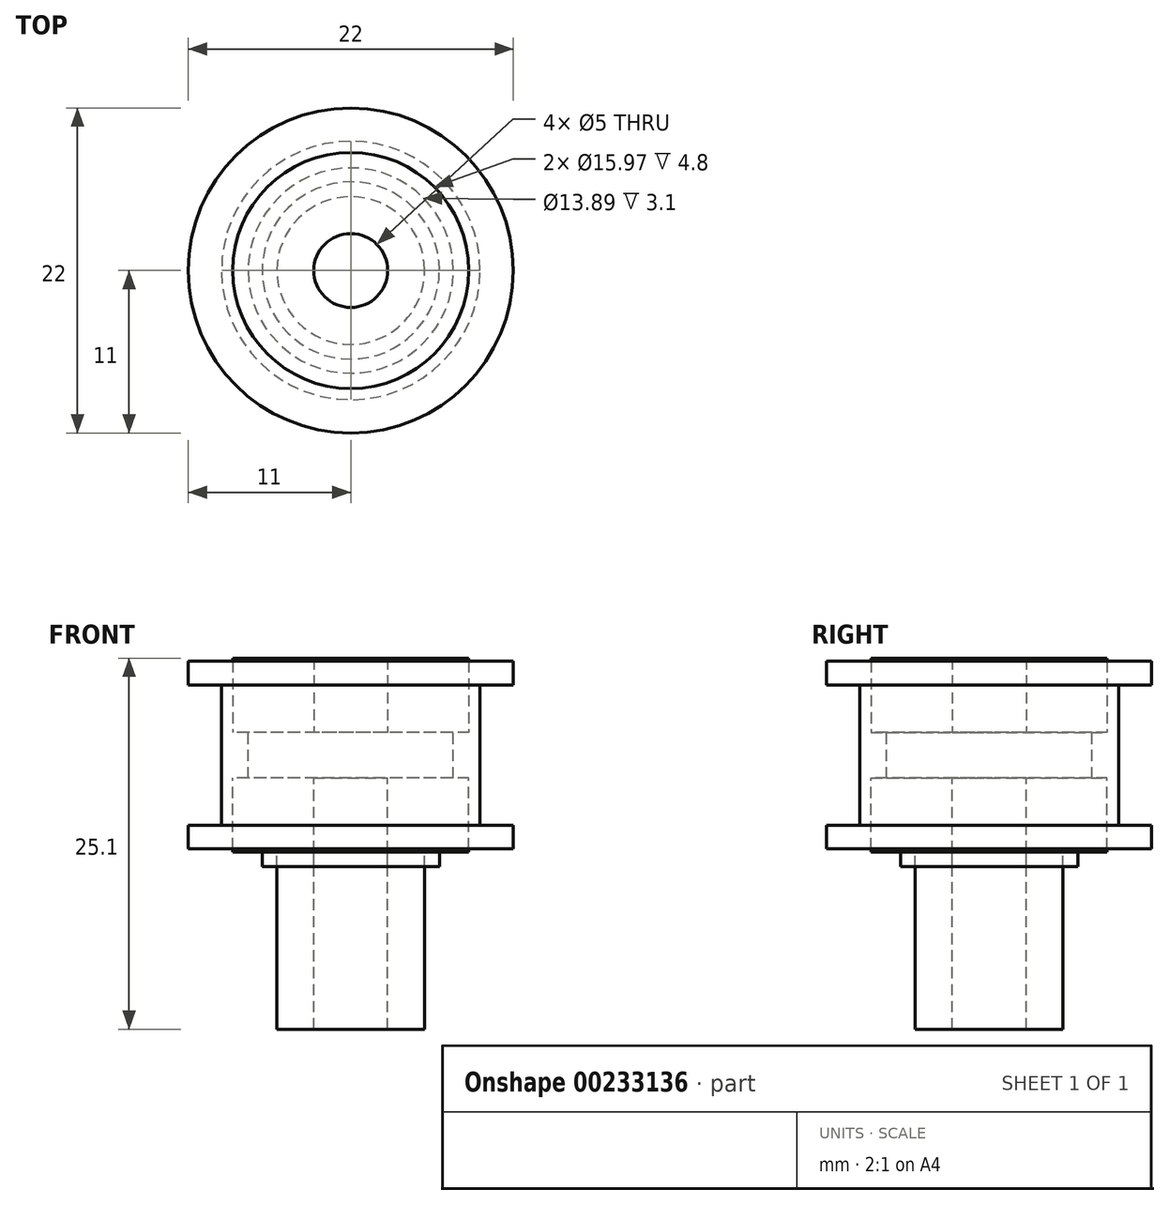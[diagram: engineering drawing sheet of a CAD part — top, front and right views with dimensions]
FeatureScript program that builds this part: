
annotation { "Feature Type Name" : "Feature", "Feature Type Description" : "" }
export const myFeature = defineFeature(function(context is Context, id is Id, definition is map)
    precondition{}
    {
        {
            var Q0;
            Q0=qCreatedBy(makeId("Right.planeOp"),FACE);
            var sketch = newSketch(context, id + "F0", { "sketchPlane" : qUnion([Q0])});
            skLineSegment(sketch, "E0", {"start": v(11, 6.35) * mm, "end": v(7.99, 6.35) * mm});
            skLineSegment(sketch, "E1", {"start": v(7.99, 6.35) * mm, "end": v(7.99, 1.55) * mm});
            skLineSegment(sketch, "E2", {"start": v(7.99, 1.55) * mm, "end": v(6.95, 1.55) * mm});
            skLineSegment(sketch, "E3", {"start": v(6.95, 1.55) * mm, "end": v(6.95, 0) * mm});
            skLineSegment(sketch, "E4", {"start": v(8.75, 0) * mm, "end": v(8.75, 4.75) * mm});
            skLineSegment(sketch, "E5", {"start": v(8.75, 4.75) * mm, "end": v(11, 4.75) * mm});
            skLineSegment(sketch, "E6", {"start": v(11, 4.75) * mm, "end": v(11, 6.35) * mm});
            skLineSegment(sketch, "E7", {"start": v(0, 6.35) * mm, "end": v(0, -6.95) * mm, "construction": true});
            skLineSegment(sketch, "E8", {"start": v(0, 0) * mm, "end": v(8.75, 0) * mm, "construction": true});
            skPoint(sketch, "E8.endSnap0", {"position": v(8.75, 0) * mm});
            skPoint(sketch, "E8.endSnap1", {"position": v(6.95, 0) * mm});
            skLineSegment(sketch, "E9.MirrorCS", {"start": v(7.99, -1.55) * mm, "end": v(6.95, -1.55) * mm});
            skLineSegment(sketch, "E10.MirrorCS", {"start": v(8.75, -4.75) * mm, "end": v(11, -4.75) * mm});
            skLineSegment(sketch, "E11.MirrorCS", {"start": v(8.75, 0) * mm, "end": v(8.75, -4.75) * mm});
            skLineSegment(sketch, "E12.MirrorCS", {"start": v(7.99, -6.35) * mm, "end": v(7.99, -1.55) * mm});
            skLineSegment(sketch, "E13.MirrorCS", {"start": v(11, -6.35) * mm, "end": v(7.99, -6.35) * mm});
            skLineSegment(sketch, "E14.MirrorCS", {"start": v(6.95, -1.55) * mm, "end": v(6.95, 0) * mm});
            skLineSegment(sketch, "E15.MirrorCS", {"start": v(11, -4.75) * mm, "end": v(11, -6.35) * mm});
            skSolve(sketch);
        }
        {
            var Q0;
            Q0 = qSketchRegion(id + "F0", true);
            var Q1;
            Q1=sQuery(id+"F0.wireOp",EDGE,"E7");
            revolve(context, id + "F1", {"surfaceOperationType" : NewSurfaceOperationType.NEW, "entities" : qUnion([Q0]), "axis" : qUnion([Q1]), "revolveType" : RevolveType.FULL});
        }
        {
            var Q0;
            Q0=makeQuery(id+"F1.opRevolve","SWEPT_FACE",FACE,{"disambiguationData":[OSD([sQuery(id+"F0.wireOp",EDGE,"E2")])]});
            var sketch = newSketch(context, id + "F2", { "sketchPlane" : qUnion([Q0])});
            skCircle(sketch, "E16.0", {"center": v(0, 0) * mm, "radius": 7.99 * mm});
            skCircle(sketch, "E17", {"center": v(0, 0) * mm, "radius": 2.5 * mm});
            skSolve(sketch);
        }
        {
            var Q0;
            Q0 = qSketchRegion(id + "F2", true);
            extrude(context, id + "F3", {"entities" : qUnion([Q0]), "depth" : 5 * mm, "offsetDistance" : 25 * mm});
        }
        {
            var Q0;
            Q0=makeQuery(id+"F1.opRevolve","SWEPT_FACE",FACE,{"disambiguationData":[OSD([sQuery(id+"F0.wireOp",EDGE,"E9.MirrorCS")])]});
            var sketch = newSketch(context, id + "F4", { "sketchPlane" : qUnion([Q0])});
            skCircle(sketch, "E18.0", {"center": v(0, 0) * mm, "radius": 7.99 * mm});
            skCircle(sketch, "E18.1", {"center": v(0, 0) * mm, "radius": 2.5 * mm});
            skSolve(sketch);
        }
        {
            var Q0;
            Q0 = qSketchRegion(id + "F4", true);
            extrude(context, id + "F5", {"entities" : qUnion([Q0]), "depth" : 5 * mm, "offsetDistance" : 25 * mm});
        }
        {
            var Q0;
            Q0=makeQuery(id+"F5.opExtrude","CAP_FACE",FACE,{"disambiguationData":[OSD([sQuery(id+"F4.wireOp",EDGE,"E18.0"),sQuery(id+"F4.wireOp",EDGE,"E18.1")])],"isStart":false});
            var sketch = newSketch(context, id + "F6", { "sketchPlane" : qUnion([Q0])});
            skCircle(sketch, "E19.0", {"center": v(0, 0) * mm, "radius": 2.5 * mm});
            skCircle(sketch, "E20", {"center": v(0, 0) * mm, "radius": 5 * mm});
            skSolve(sketch);
        }
        {
            var Q0;
            Q0 = qSketchRegion(id + "F6", true);
            extrude(context, id + "F7", {"entities" : qUnion([Q0]), "depth" : 12 * mm, "offsetDistance" : 25 * mm});
        }
        {
            var Q0;
            Q0=makeQuery(id+"F5.opExtrude","CAP_FACE",FACE,{"disambiguationData":[OSD([sQuery(id+"F4.wireOp",EDGE,"E18.0"),sQuery(id+"F4.wireOp",EDGE,"E18.1")])],"isStart":false});
            var sketch = newSketch(context, id + "F8", { "sketchPlane" : qUnion([Q0])});
            skCircle(sketch, "E21.0", {"center": v(0, 0) * mm, "radius": 2.5 * mm});
            skCircle(sketch, "E22", {"center": v(0, 0) * mm, "radius": 6 * mm});
            skSolve(sketch);
        }
        {
            var Q0;
            Q0 = qSketchRegion(id + "F8", true);
            extrude(context, id + "F9", {"entities" : qUnion([Q0]), "depth" : 1 * mm, "offsetDistance" : 25 * mm});
        }
    });
